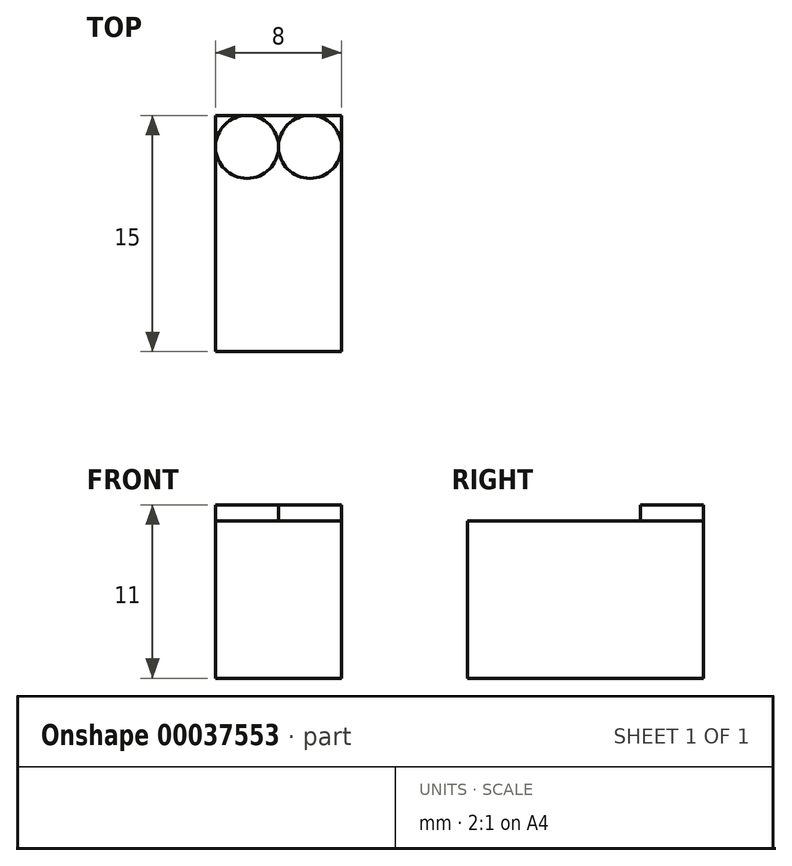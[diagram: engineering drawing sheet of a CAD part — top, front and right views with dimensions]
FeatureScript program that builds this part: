
annotation { "Feature Type Name" : "Feature", "Feature Type Description" : "" }
export const myFeature = defineFeature(function(context is Context, id is Id, definition is map)
    precondition{}
    {
        {
            var Q0;
            Q0=qCreatedBy(makeId("Top.planeOp"),FACE);
            var sketch = newSketch(context, id + "F0", { "sketchPlane" : qUnion([Q0])});
            skLineSegment(sketch, "E0.bottom", {"start": v(4.24, 4.74) * mm, "end": v(12.24, 4.74) * mm});
            skLineSegment(sketch, "E0.top", {"start": v(4.24, 19.74) * mm, "end": v(12.24, 19.74) * mm});
            skLineSegment(sketch, "E0.left", {"start": v(4.24, 4.74) * mm, "end": v(4.24, 19.74) * mm});
            skLineSegment(sketch, "E0.right", {"start": v(12.24, 4.74) * mm, "end": v(12.24, 19.74) * mm});
            skSolve(sketch);
        }
        {
            var Q0;
            Q0=makeQuery(id+"F0.imprint","IMPRINT",FACE,{"disambiguationData":[TD([[makeQuery(id+"F0.imprint","IMPRINT",EDGE,{"derivedFrom":sQuery(id+"F0.wireOp",EDGE,"E0.bottom")}),1.0]])]});
            extrude(context, id + "F1", {"entities" : qUnion([Q0]), "depth" : 10 * mm});
        }
        {
            var Q0;
            Q0=makeQuery(id+"F1.opExtrude","CAP_FACE",FACE,{"disambiguationData":[OSD([sQuery(id+"F0.wireOp",EDGE,"E0.bottom"),sQuery(id+"F0.wireOp",EDGE,"E0.top"),sQuery(id+"F0.wireOp",EDGE,"E0.left"),sQuery(id+"F0.wireOp",EDGE,"E0.right")])],"isStart":false});
            var sketch = newSketch(context, id + "F2", { "sketchPlane" : qUnion([Q0])});
            skCircle(sketch, "E1", {"center": v(6.24, 17.74) * mm, "radius": 2 * mm});
            skSolve(sketch);
        }
        {
            var Q0;
            Q0=makeQuery(id+"F1.opExtrude","CAP_FACE",FACE,{"disambiguationData":[OSD([sQuery(id+"F0.wireOp",EDGE,"E0.bottom"),sQuery(id+"F0.wireOp",EDGE,"E0.top"),sQuery(id+"F0.wireOp",EDGE,"E0.left"),sQuery(id+"F0.wireOp",EDGE,"E0.right")])],"isStart":false});
            var sketch = newSketch(context, id + "F3", { "sketchPlane" : qUnion([Q0])});
            skCircle(sketch, "E2", {"center": v(10.24, 17.74) * mm, "radius": 2 * mm});
            skSolve(sketch);
        }
        {
            var Q0;
            Q0 = qSketchRegion(id + "F2", true);
            extrude(context, id + "F4", {"entities" : qUnion([Q0]), "operationType" : NewBodyOperationType.ADD, "depth" : 1 * mm});
        }
        {
            var Q0;
            {var subQ0=sQuery(id+"F3.wireOp",EDGE,"E2");var subQ2=makeQuery(id+"F3.imprint","INTERSECT",VERTEX,{"derivedFrom":[makeQuery(id+"F1.opExtrude","CAP_EDGE",EDGE,{"disambiguationData":[OSD([sQuery(id+"F0.wireOp",EDGE,"E0.top")])],"isStart":false}),subQ0]});Q0=makeQuery(id+"F3.imprint","IMPRINT",FACE,{"disambiguationData":[TD([[makeQuery(id+"F3.imprint","IMPRINT",EDGE,{"disambiguationData":[TD([[subQ2,1.0]])],"derivedFrom":subQ0}),1.0]])]});}
            extrude(context, id + "F5", {"entities" : qUnion([Q0]), "depth" : 1 * mm});
        }
    });
